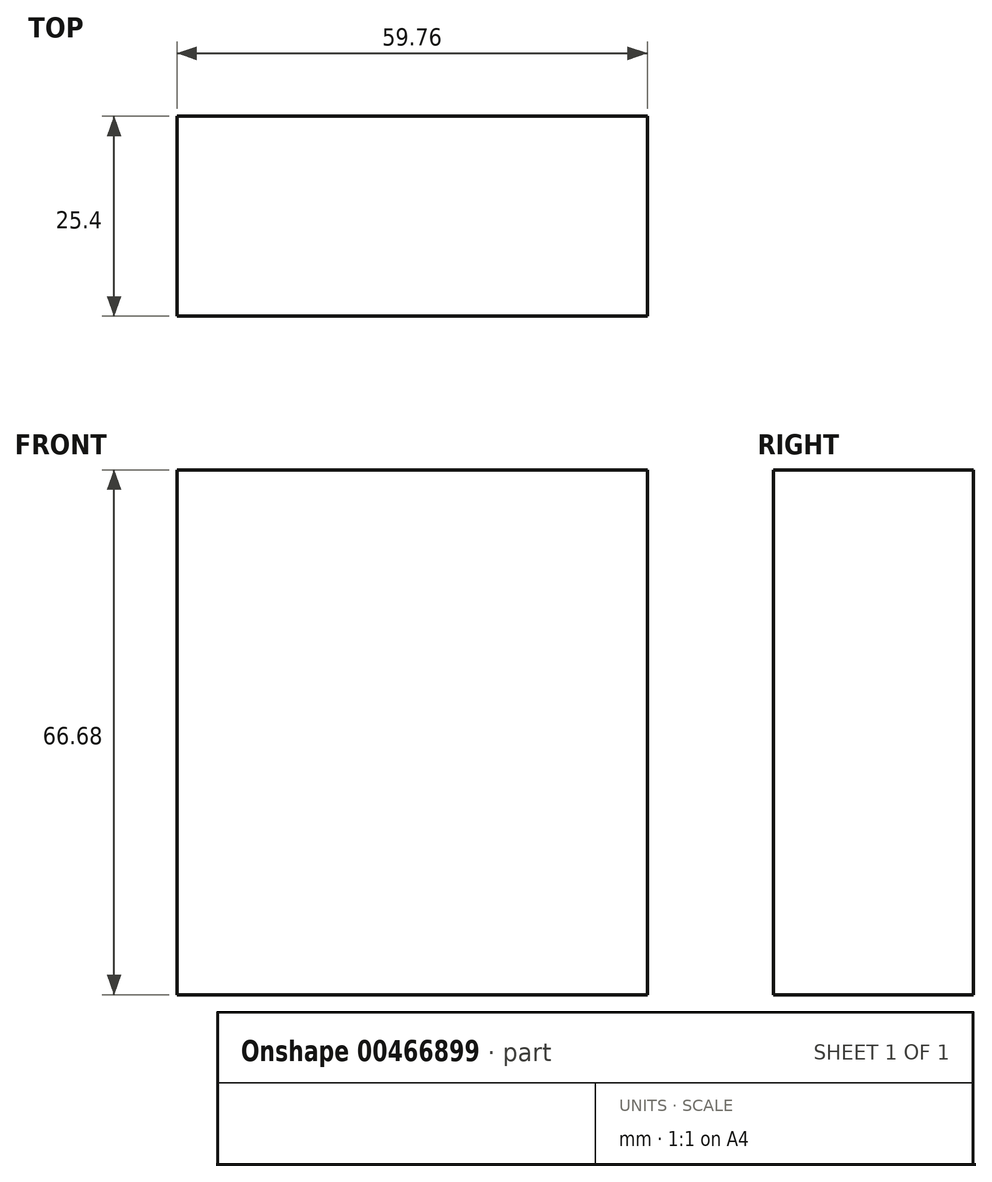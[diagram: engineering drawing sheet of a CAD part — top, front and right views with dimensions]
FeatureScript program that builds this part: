
annotation { "Feature Type Name" : "Feature", "Feature Type Description" : "" }
export const myFeature = defineFeature(function(context is Context, id is Id, definition is map)
    precondition{}
    {
        {
            var Q0;
            Q0=qCreatedBy(makeId("Front.planeOp"),FACE);
            var sketch = newSketch(context, id + "F0", { "sketchPlane" : qUnion([Q0])});
            skLineSegment(sketch, "E0.bottom", {"start": v(37.5, 50.72) * mm, "end": v(-22.25, 50.72) * mm});
            skLineSegment(sketch, "E0.top", {"start": v(37.5, -15.96) * mm, "end": v(-22.25, -15.96) * mm});
            skLineSegment(sketch, "E0.left", {"start": v(37.5, 50.72) * mm, "end": v(37.5, -15.96) * mm});
            skLineSegment(sketch, "E0.right", {"start": v(-22.25, 50.72) * mm, "end": v(-22.25, -15.96) * mm});
            skLineSegment(sketch, "E1.bottom", {"start": v(21.12, 50.72) * mm, "end": v(30.96, 50.72) * mm});
            skLineSegment(sketch, "E1.top", {"start": v(21.12, 102) * mm, "end": v(30.96, 102) * mm});
            skLineSegment(sketch, "E1.left", {"start": v(21.12, 50.72) * mm, "end": v(21.12, 102) * mm});
            skLineSegment(sketch, "E1.right", {"start": v(30.96, 50.72) * mm, "end": v(30.96, 102) * mm});
            skSolve(sketch);
        }
        {
            var Q0;
            Q0=makeQuery(id+"F0.imprint","IMPRINT",FACE,{"disambiguationData":[TD([[makeQuery(id+"F0.imprint","IMPRINT",EDGE,{"derivedFrom":sQuery(id+"F0.wireOp",EDGE,"E0.top")}),-1.0]])]});
            extrude(context, id + "F1", {"entities" : qUnion([Q0]), "depth" : 25.4 * mm});
        }
    });
